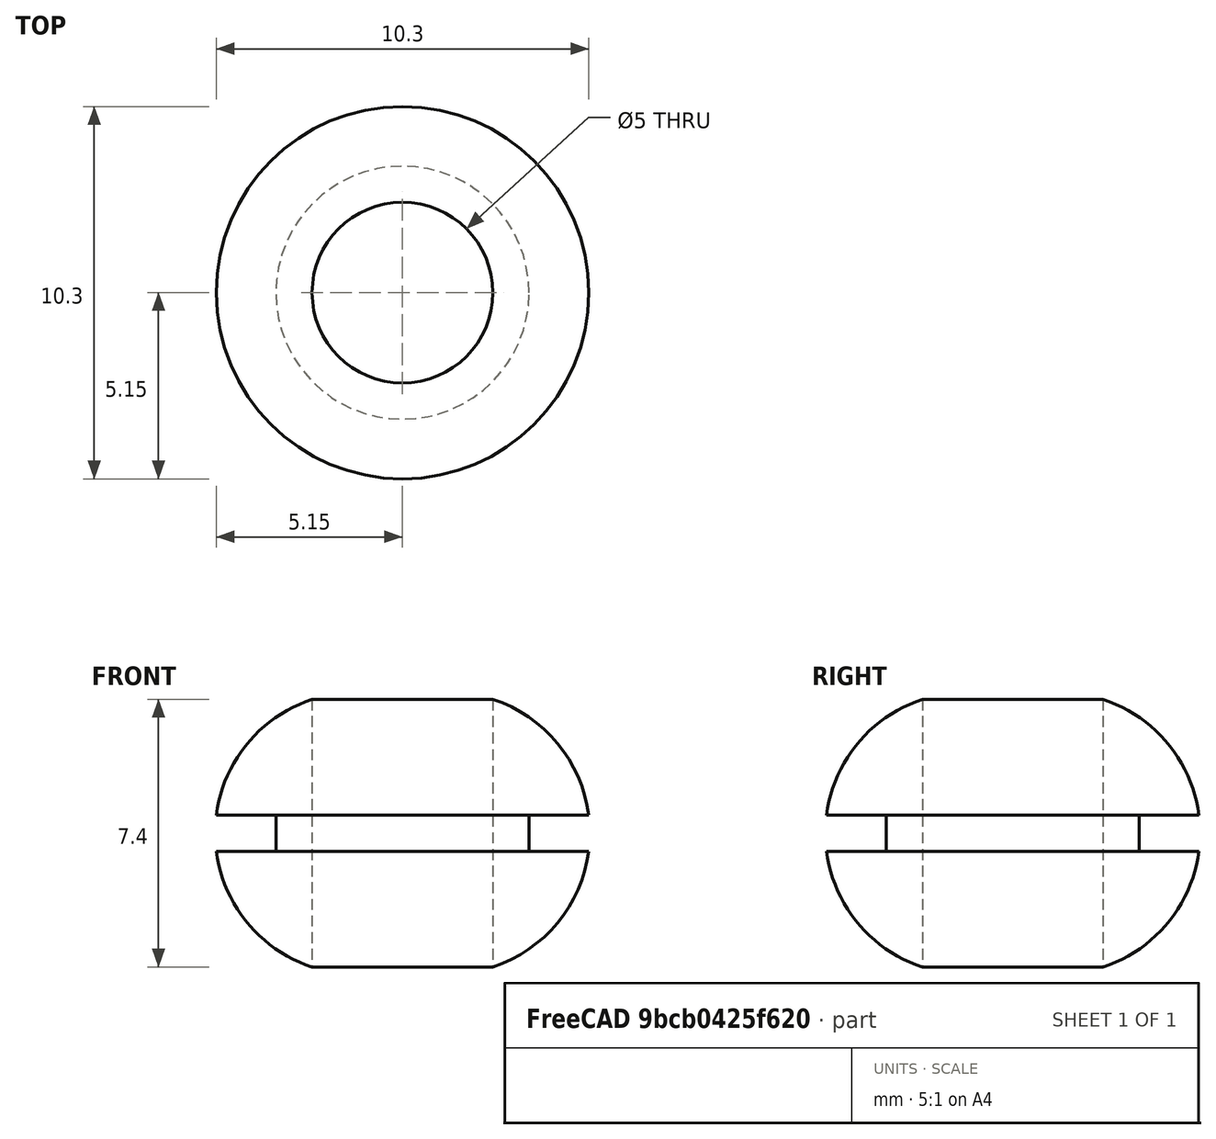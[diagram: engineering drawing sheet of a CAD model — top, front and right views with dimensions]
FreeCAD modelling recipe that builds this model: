
FCSTD DOCUMENT  (FreeCAD 0.15R4671 (Git))
Label: G9
License: CreativeCommons Attribution-ShareAlike
LicenseURL: http://creativecommons.org/licenses/by-sa/4.0/
objects: App::FeaturePython×5, App::DocumentObjectGroup×3, Part::Part2DObjectPython×3, Drawing::FeatureViewPart×3, Drawing::FeatureViewPython×3, Sketcher::SketchObject×1, PartDesign::Revolution×1, Drawing::FeaturePage×1
note: 6 computed .brp shape members not serialized (recipe doc carries the construction recipe); baked Part::Feature solids carry a one-line shape summary decoded from their .brp

FEATURE [Sketcher::SketchObject] Sketch
  Placement = pos=(0,0,0) rot=(1,0,0;1.5708rad)
  sketch-geometry (6):
    g0: LineSegment StartX=2.5 StartY=3.7 StartZ=0 EndX=2.5 EndY=-3.7 EndZ=0
    g1: LineSegment StartX=5.15 StartY=0.5 StartZ=0 EndX=3.5 EndY=0.5 EndZ=0
    g2: LineSegment StartX=3.5 StartY=0.5 StartZ=0 EndX=3.5 EndY=-0.5 EndZ=0
    g3: LineSegment StartX=3.5 StartY=-0.5 StartZ=0 EndX=5.15 EndY=-0.5 EndZ=0
    g4: ArcOfCircle CenterX=1.28915 CenterY=0 CenterZ=0 NormalX=0 NormalY=0 NormalZ=1 Radius=3.89309 StartAngle=0.128788 EndAngle=1.25452
    g5: ArcOfCircle CenterX=1.28915 CenterY=0 CenterZ=0 NormalX=0 NormalY=0 NormalZ=1 Radius=3.89309 StartAngle=5.02866 EndAngle=6.1544
  constraints (19):
    c: Vertical(g0)
    c: Horizontal(g1)
    c: Coincident(g1,g2)
    c: Vertical(g2)
    c: Coincident(g2,g3)
    c: Horizontal(g3)
    c: Symmetric(g0,g0,g-1)
    c: Symmetric(g1,g2,g-1)
    c: DistanceX(g-1,g0) = 2.5
    c: DistanceX(g-1,g1) = 3.5
    c: DistanceX(g-1,g1) = 5.15
    c: Equal(g1,g3)
    c: DistanceY(g1,g3) = -1
    c: Coincident(g4,g0)
    c: Coincident(g4,g1)
    c: Coincident(g5,g4)
    c: Coincident(g5,g0)
    c: Coincident(g5,g3)
    c: DistanceY(g0,g0) = -7.4
FEATURE [PartDesign::Revolution] Revolution
  Angle = 360
  Axis = (0,0,1)
  Base = (0,0,0)
  Placement = pos=(0,0,0) rot=(1,0,0;1.5708rad)
  ReferenceAxis = -> Sketch [V_Axis]
  Reversed = true
  Sketch = -> Sketch
FEATURE [App::FeaturePython] Dimension002  # Draft dimension (typed FeaturePython)
  Dimline = (10,0,3)
  Direction = (0,0,0)
  Distance = 7.4
  End = (2.5,0,3.7)
  Normal = (0,-1,0)
  Start = (2.5,0,-3.7)
FEATURE [App::FeaturePython] Dimension003  # Draft dimension (typed FeaturePython)
  Dimline = (-9.98017,0,0.223137)
  Direction = (0,0,0)
  Distance = 1
  End = (0,0,0.5)
  Normal = (0,-1,0)
  Start = (0,0,-0.5)
FEATURE [App::DocumentObjectGroup] Group002  label="Cotas_Z"
  Group = -> [Dimension002,Dimension003]
FEATURE [Part::Part2DObjectPython] Line  # Draft 2D object (typed FeaturePython)
  ChamferSize = 0
  Closed = false
  End = (-5.15,0,-0.5)
  FilletRadius = 0
  Length = 1
  MakeFace = true
  Points = (2) [(-5.15,1.11022e-16,0.5),(-5.15,-1.11022e-16,-0.5)]
  Start = (-5.15,0,0.5)
FEATURE [Part::Part2DObjectPython] Line001  # Draft 2D object (typed FeaturePython)
  ChamferSize = 0
  Closed = false
  End = (5.15,0,-0.5)
  FilletRadius = 0
  Length = 1
  MakeFace = true
  Points = (2) [(5.15,3.33067e-16,0.5),(5.15,-3.33067e-16,-0.5)]
  Start = (5.15,0,0.5)
FEATURE [App::FeaturePython] Dimension004  # Draft dimension (typed FeaturePython)
  Dimline = (0,-8,0)
  Direction = (0,0,0)
  Distance = 10.3
  End = (5.15,0,0)
  Normal = (0,0,1)
  Start = (-5.15,0,0)
FEATURE [App::FeaturePython] Dimension005  # Draft dimension (typed FeaturePython)
  Dimline = (-1,0,6)
  Direction = (0,0,0)
  Distance = 5
  End = (2.5,0,3.7)
  Normal = (0,-1,0)
  Start = (-2.5,0,3.7)
FEATURE [App::DocumentObjectGroup] Group  label="Cota_Agujero"
  Group = -> [Dimension005]
FEATURE [Drawing::FeatureViewPart] Ortho  label="Ortho_0_0"
  Direction = (0,0,1)
  HiddenWidth = 0.15
  LineWidth = 0.35
  Rotation = 0
  Scale = 5
  ShowHiddenLines = false
  ShowSmoothLines = false
  Source = -> Revolution
  Tolerance = 0.05
  ViewResult = <g id="Ortho_0_0"\n   transform="rotate(0,201.75,57.58) translate(201.75,57.58) scale(5,5)"\n  >\n<g   stroke="rgb(0, 0, 0)"\n   stroke-width="0.07"\n   stroke-linecap="butt"\n   stroke-linejoin="miter"\n   fill="none"\n   transform="scale(1,-1)"\n  >\n<circle cx ="0" cy ="2.22045e-016" r ="5.15" /><circle cx ="0" cy ="1.64313e-015" r ="2.5" /></g>\n</g>
  Visible = true
  X = 201.75
  Y = 57.58
FEATURE [Drawing::FeatureViewPart] Ortho001  label="Ortho_0_-1"
  Direction = (0,-1,0)
  HiddenWidth = 0.15
  LineWidth = 0.35
  Rotation = 90
  Scale = 5
  ShowHiddenLines = false
  ShowSmoothLines = false
  Source = -> Revolution
  Tolerance = 0.05
  ViewResult = <g id="Ortho_0_-1"\n   transform="rotate(90,201.75,123.667) translate(201.75,123.667) scale(5,5)"\n  >\n<g   stroke="rgb(0, 0, 0)"\n   stroke-width="0.07"\n   stroke-linecap="butt"\n   stroke-linejoin="miter"\n   fill="none"\n   transform="scale(1,-1)"\n  >\n<path d="M-0.5,-5.15 C-1.23337,-5.05651 -1.92351,-4.74805 -2.46615,-4.3015  C-3.05545,-3.81957 -3.47698,-3.18386 -3.7,-2.5 " /><path d="M3.7,-2.5 C3.48121,-3.17073 3.0717,-3.79506 2.49991,-4.27355  C1.95196,-4.73504 1.24872,-5.05463 0.5,-5.15 " /><path id= "3" d=" M -0.5 -3.5 L 0.5 -3.5 " />\n</g>\n<g   stroke="rgb(0, 0, 0)"\n   stroke-width="0.07"\n   stroke-linecap="butt"\n   stroke-linejoin="miter"\n   fill="none"\n   transform="scale(1,-1)"\n  >\n<path d="M-0.5,5.15 L-0.5,5.02088  L-0.5,4.63999  L-0.5,4.02643  L-0.5,3.21097  L-0.5,2.2345  L-0.5,1.14598  L-0.5,4.26369e-016  L-0.5,-1.14598  L-0.5,-2.2345  L-0.5,-3.21097  L-0.5,-4.02643  L-0.5,-4.63999  L-0.5,-5.02088  L-0.5,-5.15 " /><path d="M-3.7,2.5 L-3.7,2.43732  L-3.7,2.25242  L-3.7,1.95458  L-3.7,1.55872  L-3.7,1.08471  L-3.7,0.556302  L-3.7,1.52976e-015  L-3.7,-0.556302  L-3.7,-1.08471  L-3.7,-1.55872  L-3.7,-1.95458  L-3.7,-2.25242  L-3.7,-2.43732  L-3.7,-2.5 " /><path d="M-0.5 5.15 A3.89309 3.89309 0 0 1 -3.7 2.5" /><path d="M3.7,2.5 L3.7,2.43732  L3.7,2.25242  L3.7,1.95458  L3.7,1.55872  L3.7,1.08471  L3.7,0.556302  L3.7,-1.2236e-015  L3.7,-0.556302  L3.7,-1.08471  L3.7,-1.55872  L3.7,-1.95458  L3.7,-2.25242  L3.7,-2.43732  L3.7,-2.5 " /><path d="M0.5,5.15 L0.5,5.02088  L0.5,4.63999  L0.5,4.02643  L0.5,3.21097  L0.5,2.2345  L0.5,1.14598  L0.5,2.04324e-016  L0.5,-1.14598  L0.5,-2.2345  L0.5,-3.21097  L0.5,-4.02643  L0.5,-4.63999  L0.5,-5.02088  L0.5,-5.15 " /><path d="M3.7 2.5 A3.89309 3.89309 0 0 1 0.5 5.15" /><path id= "7" d=" M -0.5 3.5 L 0.5 3.5 " />\n</g>\n</g>
  Visible = true
  X = 201.75
  Y = 123.667
FEATURE [Drawing::FeatureViewPart] Ortho002  label="Ortho_-1_-1"
  Direction = (-0.57735,-0.57735,0.57735)
  HiddenWidth = 0.15
  LineWidth = 0.35
  Rotation = -60
  Scale = 5
  ShowHiddenLines = false
  ShowSmoothLines = false
  Source = -> Revolution
  Tolerance = 0.05
  ViewResult = <blob: 2068 chars omitted>
  Visible = true
  X = 98
  Y = 123.667
FEATURE [Drawing::FeatureViewPython] ViewGroup002  # drawing view (typed FeaturePython)
  Direction = (0,-1,0)
  FillStyle = 0
  FontSize = 12
  LineStyle = 0
  LineWidth = 0.5
  Rotation = 90
  Scale = 5
  Source = -> Group002
  ViewResult = <blob: 2051 chars omitted>
  Visible = true
  X = 201.75
  Y = 123.67
FEATURE [Drawing::FeatureViewPython] ViewGroup  # drawing view (typed FeaturePython)
  Direction = (-0.58,-0.58,0.58)
  FillStyle = 0
  FontSize = 12
  LineStyle = 0
  LineWidth = 0.5
  Rotation = -60
  Scale = 5
  Source = -> Group
  ViewResult = <g id="ViewGroup" transform="rotate(-60.0,98.0,123.67) translate(98.0,123.67) scale(5.0,-5.0)"><path d="M 0.848528137424 2.53113940088 L 2.47487373415 3.47011046894 L 6.01040764009 1.42886901662 L 4.38406204336 0.489897948557" fill="none" stroke="#0054ff" stroke-width="0.1 px" style="stroke-width:0.1;stroke-miterlimit:4;stroke-dasharray:none" freecad:basepoint1="0.848528137424 2.53113940088" freecad:basepoint2="4.38406204336 0.489897948557" freecad:dimpoint="2.47487373415 3.47011046894"/>\n<path transform="rotate(150.0,2.47487373415,3.47011046894) translate(2.47487373415,3.47011046894) scale(0.666666666667,0.666666666667)" freecad:skip="1" fill="#0054ff" stroke="none" style="stroke-miterlimit:4;stroke-dasharray:none" d="M 0 0 L 4 1 L 4 -1 Z"/>\n<path transform="rotate(330.0,6.01040764009,1.42886901662) translate(6.01040764009,1.42886901662) scale(0.666666666667,0.666666666667)" freecad:skip="1" fill="#0054ff" stroke="none" style="stroke-miterlimit:4;stroke-dasharray:none" d="M 0 0 L 4 1 L 4 -1 Z"/>\n<text fill="#0054ff" font-size="1.2" style="text-anchor:middle;text-align:center;font-family:" transform="rotate(-30.0,4.59619407771,2.65361388802) translate(4.59619407771,2.65361388802) scale(1,-1) " freecad:skip="1">\n5 </text>\n</g>
  Visible = true
  X = 98
  Y = 123.67
FEATURE [Part::Part2DObjectPython] Line002  # Draft 2D object (typed FeaturePython)
  ChamferSize = 0
  Closed = false
  End = (-3.5,0,-0.5)
  FilletRadius = 0
  Length = 1
  MakeFace = true
  Points = (2) [(-3.5,1.11022e-16,0.5),(-3.5,-1.11022e-16,-0.5)]
  Start = (-3.5,0,0.5)
FEATURE [App::FeaturePython] Dimension  # Draft dimension (typed FeaturePython)
  Dimline = (0.844398,7.98372,0)
  Direction = (0,0,0)
  Distance = 7
  End = (-3.5,0,0)
  Normal = (0,0,1)
  Start = (3.5,0,0)
FEATURE [App::DocumentObjectGroup] Group001  label="Cotas_XY"
  Group = -> [Line001,Line,Dimension004,Dimension,Line002]
FEATURE [Drawing::FeatureViewPython] ViewGroup001  # drawing view (typed FeaturePython)
  Direction = (0,0,0)
  FillStyle = 0
  FontSize = 12
  LineStyle = 0
  LineWidth = 0.5
  Rotation = 0
  Scale = 5
  Source = -> Group001
  ViewResult = <blob: 2425 chars omitted>
  Visible = true
  X = 201.75
  Y = 57.58
FEATURE [Drawing::FeaturePage] Page
  EditableTexts = Marcelo | Marcelo | VioMar | type | G9 |  19-07-2015
  Group = -> [Ortho,Ortho001,Ortho002,ViewGroup001,ViewGroup002,ViewGroup]
  Template = C:/Program Files/FreeCAD 0.15/data/Mod/Drawing/Templates/A4_Landscape_ISO7200.svg
